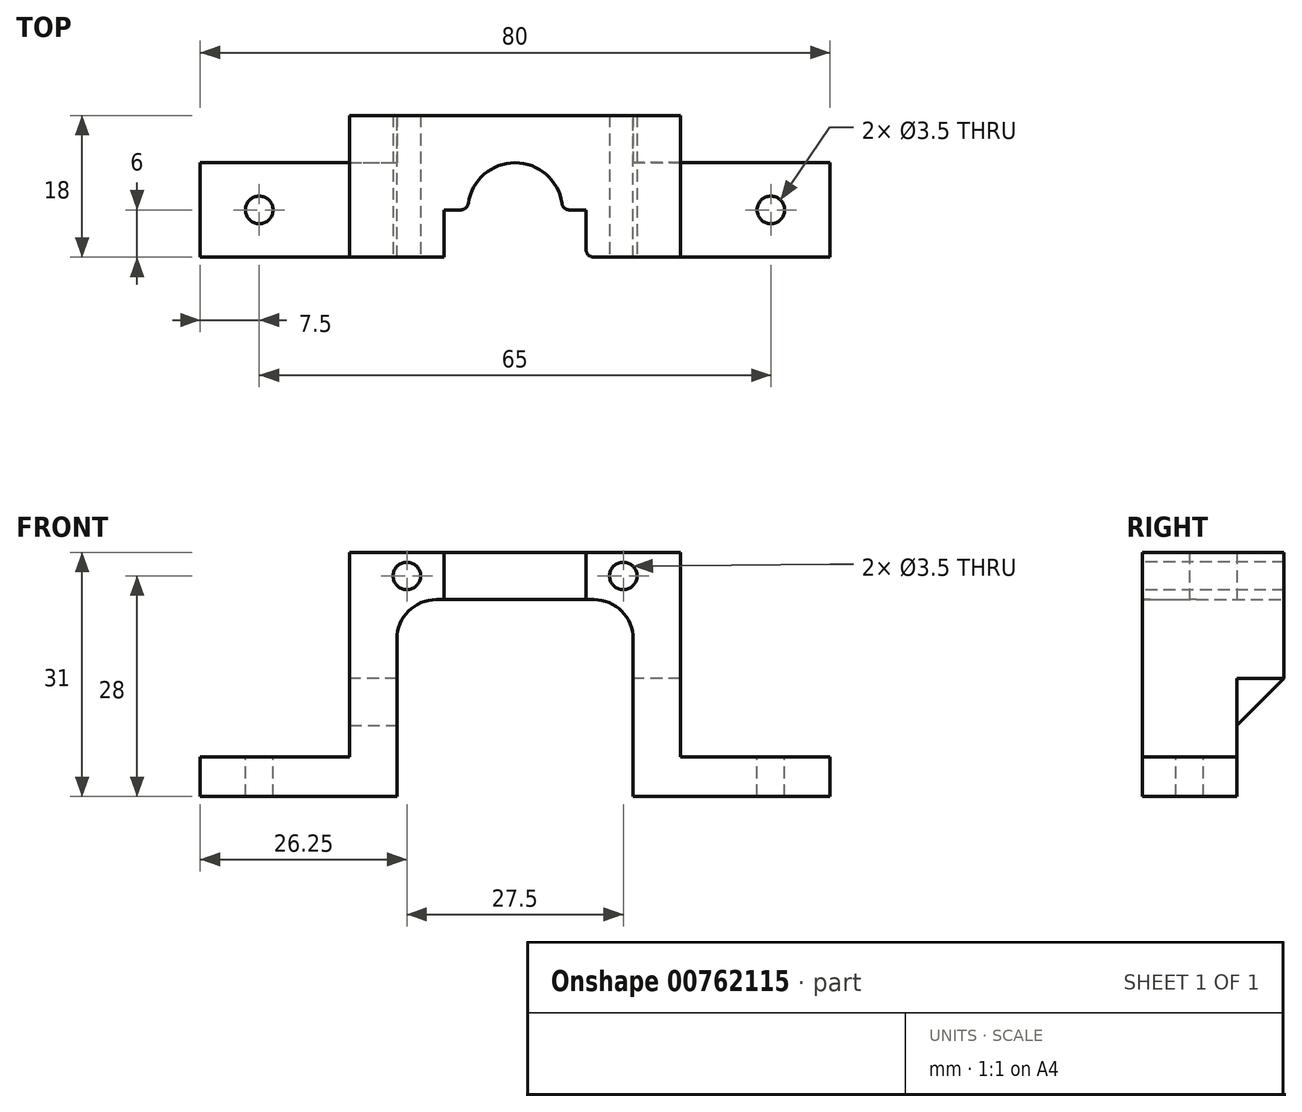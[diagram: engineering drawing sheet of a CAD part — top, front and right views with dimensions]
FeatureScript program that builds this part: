
annotation { "Feature Type Name" : "Feature", "Feature Type Description" : "" }
export const myFeature = defineFeature(function(context is Context, id is Id, definition is map)
    precondition{}
    {
        {
            var Q0;
            Q0=qCreatedBy(makeId("Front.planeOp"),FACE);
            var sketch = newSketch(context, id + "F0", { "sketchPlane" : qUnion([Q0])});
            skLineSegment(sketch, "E0", {"start": v(0, 0) * mm, "end": v(25, 0) * mm});
            skLineSegment(sketch, "E1", {"start": v(25, 0) * mm, "end": v(25, 25) * mm});
            skLineSegment(sketch, "E2", {"start": v(25, 25) * mm, "end": v(55, 25) * mm});
            skLineSegment(sketch, "E3", {"start": v(55, 25) * mm, "end": v(55, 0) * mm});
            skLineSegment(sketch, "E4", {"start": v(55, 0) * mm, "end": v(80, 0) * mm});
            skLineSegment(sketch, "E5", {"start": v(80, 0) * mm, "end": v(80, 5) * mm});
            skLineSegment(sketch, "E6", {"start": v(80, 5) * mm, "end": v(61, 5) * mm});
            skLineSegment(sketch, "E7", {"start": v(61, 5) * mm, "end": v(61, 31) * mm});
            skLineSegment(sketch, "E8", {"start": v(61, 31) * mm, "end": v(19, 31) * mm});
            skLineSegment(sketch, "E9", {"start": v(19, 31) * mm, "end": v(19, 5) * mm});
            skLineSegment(sketch, "E10", {"start": v(19, 5) * mm, "end": v(0, 5) * mm});
            skLineSegment(sketch, "E11", {"start": v(0, 5) * mm, "end": v(0, 0) * mm});
            skPoint(sketch, "E12", {"position": v(40, 25) * mm});
            skPoint(sketch, "E13", {"position": v(40, 31) * mm});
            skLineSegment(sketch, "E14", {"start": v(0, 0) * mm, "end": v(80, 0) * mm, "construction": true});
            skPoint(sketch, "E15", {"position": v(40, 0) * mm});
            skSolve(sketch);
        }
        {
            var Q0;
            Q0=makeQuery(id+"F0.imprint","IMPRINT",FACE,{"disambiguationData":[TD([[makeQuery(id+"F0.imprint","IMPRINT",EDGE,{"derivedFrom":sQuery(id+"F0.wireOp",EDGE,"E0")}),1.0]])]});
            extrude(context, id + "F1", {"entities" : qUnion([Q0]), "depth" : 12 * mm, "offsetDistance" : 25 * mm});
        }
        {
            var Q0;
            Q0=makeQuery(id+"F1.opExtrude","CAP_FACE",FACE,{"disambiguationData":[OSD([sQuery(id+"F0.wireOp",EDGE,"E0"),sQuery(id+"F0.wireOp",EDGE,"E1"),sQuery(id+"F0.wireOp",EDGE,"E2"),sQuery(id+"F0.wireOp",EDGE,"E3"),sQuery(id+"F0.wireOp",EDGE,"E4"),sQuery(id+"F0.wireOp",EDGE,"E5"),sQuery(id+"F0.wireOp",EDGE,"E6"),sQuery(id+"F0.wireOp",EDGE,"E7"),sQuery(id+"F0.wireOp",EDGE,"E8"),sQuery(id+"F0.wireOp",EDGE,"E9"),sQuery(id+"F0.wireOp",EDGE,"E10"),sQuery(id+"F0.wireOp",EDGE,"E11")])],"isStart":true});
            var sketch = newSketch(context, id + "F2", { "sketchPlane" : qUnion([Q0])});
            skLineSegment(sketch, "E16", {"start": v(-61, 15) * mm, "end": v(-55, 15) * mm});
            skLineSegment(sketch, "E17", {"start": v(-55, 15) * mm, "end": v(-55, 25) * mm});
            skLineSegment(sketch, "E18", {"start": v(-55, 25) * mm, "end": v(-25, 25) * mm});
            skLineSegment(sketch, "E19", {"start": v(-25, 25) * mm, "end": v(-25, 15) * mm});
            skPoint(sketch, "E19.endSnap0", {"position": v(-25, 12.5) * mm});
            skLineSegment(sketch, "E20", {"start": v(-25, 15) * mm, "end": v(-19, 15) * mm});
            skLineSegment(sketch, "E21", {"start": v(-19, 15) * mm, "end": v(-19, 31) * mm});
            skLineSegment(sketch, "E22", {"start": v(-19, 31) * mm, "end": v(-61, 31) * mm});
            skLineSegment(sketch, "E23", {"start": v(-61, 31) * mm, "end": v(-61, 15) * mm});
            skSolve(sketch);
        }
        {
            var Q0;
            Q0=makeQuery(id+"F2.imprint","IMPRINT",FACE,{"disambiguationData":[TD([[makeQuery(id+"F2.imprint","IMPRINT",EDGE,{"derivedFrom":sQuery(id+"F2.wireOp",EDGE,"E16")}),1.0]])]});
            extrude(context, id + "F3", {"entities" : qUnion([Q0]), "operationType" : NewBodyOperationType.ADD, "depth" : 6 * mm, "offsetDistance" : 25 * mm});
        }
        {
            var Q0;
            Q0=makeQuery(id+"F3.boolean.opBoolean","MERGE",FACE,{"derivedFrom":[makeQuery(id+"F1.opExtrude","SWEPT_FACE",FACE,{"disambiguationData":[OSD([sQuery(id+"F0.wireOp",EDGE,"E2")])]}),makeQuery(id+"F3.opExtrude","SWEPT_FACE",FACE,{"disambiguationData":[OSD([sQuery(id+"F2.wireOp",EDGE,"E18")])]})]});
            var sketch = newSketch(context, id + "F4", { "sketchPlane" : qUnion([Q0])});
            skCircle(sketch, "E24", {"center": v(40, 6) * mm, "radius": 6 * mm, "construction": true});
            skLineSegment(sketch, "E25.0.0", {"start": v(61, 12) * mm, "end": v(61, -6) * mm});
            skLineSegment(sketch, "E25.0.1", {"start": v(61, -6) * mm, "end": v(19, -6) * mm});
            skLineSegment(sketch, "E25.0.2", {"start": v(19, -6) * mm, "end": v(19, 12) * mm});
            skLineSegment(sketch, "E25.0.3", {"start": v(19, 12) * mm, "end": v(61, 12) * mm});
            skLineSegment(sketch, "E26.0.0", {"start": v(80, 0) * mm, "end": v(61, 0) * mm});
            skLineSegment(sketch, "E26.0.1", {"start": v(61, 0) * mm, "end": v(61, 12) * mm});
            skLineSegment(sketch, "E26.0.2", {"start": v(61, 12) * mm, "end": v(80, 12) * mm});
            skLineSegment(sketch, "E26.0.3", {"start": v(80, 12) * mm, "end": v(80, 0) * mm});
            skPoint(sketch, "E27", {"position": v(80, 6) * mm});
            skPoint(sketch, "E28", {"position": v(40, -6) * mm});
            skLineSegment(sketch, "E29", {"start": v(28.62, 6) * mm, "end": v(51.1, 6) * mm, "construction": true});
            skLineSegment(sketch, "E30", {"start": v(31, 12) * mm, "end": v(31, 6) * mm});
            skPoint(sketch, "E31", {"position": v(34, 6) * mm});
            skPoint(sketch, "E32", {"position": v(46, 6) * mm});
            skLineSegment(sketch, "E33", {"start": v(49, 12) * mm, "end": v(49, 6) * mm});
            skLineSegment(sketch, "E34", {"start": v(49, 6) * mm, "end": v(46, 6) * mm});
            skLineSegment(sketch, "E35", {"start": v(31, 6) * mm, "end": v(34, 6) * mm});
            skLineSegment(sketch, "E36", {"start": v(31, 12) * mm, "end": v(49, 12) * mm});
            skArc(sketch, "E37", {"start": v(34, 6) * mm, "mid": v(40, 0) * mm, "end": v(46, 6) * mm});
            skPoint(sketch, "E38", {"position": v(40, 12) * mm});
            skSolve(sketch);
        }
        {
            var Q0;
            Q0=makeQuery(id+"F4.imprint","IMPRINT",FACE,{"disambiguationData":[TD([[makeQuery(id+"F4.imprint","IMPRINT",EDGE,{"derivedFrom":sQuery(id+"F4.wireOp",EDGE,"E30")}),1.0]])]});
            extrude(context, id + "F5", {"entities" : qUnion([Q0]), "operationType" : NewBodyOperationType.REMOVE, "oppositeDirection" : true, "depth" : 25 * mm, "offsetDistance" : 25 * mm});
        }
        {
            var Q0;
            Q0=makeQuery(id+"F1.opExtrude","SWEPT_FACE",FACE,{"disambiguationData":[OSD([sQuery(id+"F0.wireOp",EDGE,"E10")])]});
            var sketch = newSketch(context, id + "F6", { "sketchPlane" : qUnion([Q0])});
            skLineSegment(sketch, "E39.0.0", {"start": v(80, 0) * mm, "end": v(61, 0) * mm});
            skLineSegment(sketch, "E39.0.1", {"start": v(61, 0) * mm, "end": v(61, -12) * mm});
            skLineSegment(sketch, "E39.0.2", {"start": v(61, -12) * mm, "end": v(80, -12) * mm});
            skLineSegment(sketch, "E39.0.3", {"start": v(80, -12) * mm, "end": v(80, 0) * mm});
            skLineSegment(sketch, "E40.0.0", {"start": v(19, 0) * mm, "end": v(0, 0) * mm});
            skLineSegment(sketch, "E40.0.1", {"start": v(0, 0) * mm, "end": v(0, -12) * mm});
            skLineSegment(sketch, "E40.0.2", {"start": v(0, -12) * mm, "end": v(19, -12) * mm});
            skLineSegment(sketch, "E40.0.3", {"start": v(19, -12) * mm, "end": v(19, 0) * mm});
            skCircle(sketch, "E41", {"center": v(7.5, -6) * mm, "radius": 1.75 * mm});
            skCircle(sketch, "E42", {"center": v(72.5, -6) * mm, "radius": 1.75 * mm});
            skPoint(sketch, "E43", {"position": v(0, -6) * mm});
            skLineSegment(sketch, "E44", {"start": v(0, 0) * mm, "end": v(80, 0) * mm, "construction": true});
            skLineSegment(sketch, "E45", {"start": v(7.5, -6) * mm, "end": v(72.5, -6) * mm, "construction": true});
            skPoint(sketch, "E46", {"position": v(40, -6) * mm});
            skPoint(sketch, "E47", {"position": v(40, 0) * mm});
            skSolve(sketch);
        }
        {
            var Q0;
            Q0=makeQuery(id+"F6.imprint","IMPRINT",FACE,{"disambiguationData":[TD([[makeQuery(id+"F6.imprint","IMPRINT",EDGE,{"derivedFrom":sQuery(id+"F6.wireOp",EDGE,"E41")}),1.0]])]});
            var Q1;
            Q1=makeQuery(id+"F6.imprint","IMPRINT",FACE,{"disambiguationData":[TD([[makeQuery(id+"F6.imprint","IMPRINT",EDGE,{"derivedFrom":sQuery(id+"F6.wireOp",EDGE,"E42")}),1.0]])]});
            extrude(context, id + "F7", {"entities" : qUnion([Q0, Q1]), "operationType" : NewBodyOperationType.REMOVE, "oppositeDirection" : true, "depth" : 25 * mm, "offsetDistance" : 25 * mm});
        }
        {
            var Q0;
            {var subQ0=sQuery(id+"F0.wireOp",EDGE,"E9");var subQ1=sQuery(id+"F0.wireOp",EDGE,"E11");var subQ2=sQuery(id+"F0.wireOp",EDGE,"E10");var subQ3=sQuery(id+"F0.wireOp",EDGE,"E0");var subQ4=sQuery(id+"F0.wireOp",EDGE,"E8");var subQ5=sQuery(id+"F0.wireOp",EDGE,"E1");var subQ6=sQuery(id+"F0.wireOp",EDGE,"E2");Q0=makeQuery(id+"F5.boolean.opBoolean","SPLIT",FACE,{"disambiguationData":[TD([makeQuery(id+"F1.opExtrude","SWEPT_FACE",FACE,{"disambiguationData":[OSD([subQ3])]})])],"derivedFrom":makeQuery(id+"F1.opExtrude","CAP_FACE",FACE,{"disambiguationData":[OSD([subQ3,subQ5,subQ6,sQuery(id+"F0.wireOp",EDGE,"E3"),sQuery(id+"F0.wireOp",EDGE,"E4"),sQuery(id+"F0.wireOp",EDGE,"E5"),sQuery(id+"F0.wireOp",EDGE,"E6"),sQuery(id+"F0.wireOp",EDGE,"E7"),subQ4,subQ0,subQ2,subQ1])],"isStart":false})});}
            var sketch = newSketch(context, id + "F8", { "sketchPlane" : qUnion([Q0])});
            skLineSegment(sketch, "E48.0.0", {"start": v(61, 31) * mm, "end": v(49, 31) * mm});
            skLineSegment(sketch, "E48.0.1", {"start": v(49, 31) * mm, "end": v(49, 25) * mm});
            skLineSegment(sketch, "E48.0.2", {"start": v(49, 25) * mm, "end": v(55, 25) * mm});
            skLineSegment(sketch, "E48.0.3", {"start": v(55, 25) * mm, "end": v(55, 0) * mm});
            skLineSegment(sketch, "E48.0.4", {"start": v(55, 0) * mm, "end": v(80, 0) * mm});
            skLineSegment(sketch, "E48.0.5", {"start": v(80, 0) * mm, "end": v(80, 5) * mm});
            skLineSegment(sketch, "E48.0.6", {"start": v(80, 5) * mm, "end": v(61, 5) * mm});
            skLineSegment(sketch, "E48.0.7", {"start": v(61, 5) * mm, "end": v(61, 31) * mm});
            skLineSegment(sketch, "E49.0.0", {"start": v(31, 25) * mm, "end": v(31, 31) * mm});
            skLineSegment(sketch, "E49.0.1", {"start": v(31, 31) * mm, "end": v(19, 31) * mm});
            skLineSegment(sketch, "E49.0.2", {"start": v(19, 31) * mm, "end": v(19, 5) * mm});
            skLineSegment(sketch, "E49.0.3", {"start": v(19, 5) * mm, "end": v(0, 5) * mm});
            skLineSegment(sketch, "E49.0.4", {"start": v(0, 5) * mm, "end": v(0, 0) * mm});
            skLineSegment(sketch, "E49.0.5", {"start": v(0, 0) * mm, "end": v(25, 0) * mm});
            skLineSegment(sketch, "E49.0.6", {"start": v(25, 0) * mm, "end": v(25, 25) * mm});
            skLineSegment(sketch, "E49.0.7", {"start": v(25, 25) * mm, "end": v(31, 25) * mm});
            skCircle(sketch, "E50", {"center": v(26.25, 28) * mm, "radius": 1.75 * mm});
            skCircle(sketch, "E51", {"center": v(53.75, 28) * mm, "radius": 1.75 * mm});
            skPoint(sketch, "E51.centerSnap0", {"position": v(31, 28) * mm});
            skLineSegment(sketch, "E52", {"start": v(26.25, 28) * mm, "end": v(53.75, 28) * mm, "construction": true});
            skPoint(sketch, "E53.0", {"position": v(40, 31) * mm});
            skPoint(sketch, "E54.0", {"position": v(49, 28) * mm});
            skPoint(sketch, "E55", {"position": v(40, 28) * mm});
            skSolve(sketch);
        }
        {
            var Q0;
            Q0=makeQuery(id+"F8.imprint","IMPRINT",FACE,{"disambiguationData":[TD([[makeQuery(id+"F8.imprint","IMPRINT",EDGE,{"derivedFrom":sQuery(id+"F8.wireOp",EDGE,"E50")}),1.0]])]});
            var Q1;
            Q1=makeQuery(id+"F8.imprint","IMPRINT",FACE,{"disambiguationData":[TD([[makeQuery(id+"F8.imprint","IMPRINT",EDGE,{"derivedFrom":sQuery(id+"F8.wireOp",EDGE,"E51")}),1.0]])]});
            extrude(context, id + "F9", {"entities" : qUnion([Q0, Q1]), "operationType" : NewBodyOperationType.REMOVE, "oppositeDirection" : true, "depth" : 25 * mm, "offsetDistance" : 25 * mm});
        }
        {
            var Q0;
            Q0=makeQuery(id+"F3.boolean.opBoolean","MERGE",EDGE,{"derivedFrom":[makeQuery(id+"F1.opExtrude","SWEPT_EDGE",EDGE,{"disambiguationData":[OSD([sQuery(id+"F0.wireOp",EDGE,"E2"),sQuery(id+"F0.wireOp",EDGE,"E3")])]}),makeQuery(id+"F3.opExtrude","SWEPT_EDGE",EDGE,{"disambiguationData":[OSD([sQuery(id+"F2.wireOp",EDGE,"E17"),sQuery(id+"F2.wireOp",EDGE,"E18")])]})]});
            var Q1;
            Q1=makeQuery(id+"F3.boolean.opBoolean","MERGE",EDGE,{"derivedFrom":[makeQuery(id+"F1.opExtrude","SWEPT_EDGE",EDGE,{"disambiguationData":[OSD([sQuery(id+"F0.wireOp",EDGE,"E1"),sQuery(id+"F0.wireOp",EDGE,"E2")])]}),makeQuery(id+"F3.opExtrude","SWEPT_EDGE",EDGE,{"disambiguationData":[OSD([sQuery(id+"F2.wireOp",EDGE,"E18"),sQuery(id+"F2.wireOp",EDGE,"E19")])]})]});
            fillet(context, id + "F10", {"entities" : qUnion([Q0, Q1]), "radius" : 5 * mm, "tangentPropagation" : true, "allowEdgeOverflow" : false});
        }
        {
            var Q0;
            Q0=makeQuery(id+"F3.opExtrude","CAP_EDGE",EDGE,{"disambiguationData":[OSD([sQuery(id+"F2.wireOp",EDGE,"E16")])],"isStart":true});
            var Q1;
            Q1=makeQuery(id+"F3.opExtrude","CAP_EDGE",EDGE,{"disambiguationData":[OSD([sQuery(id+"F2.wireOp",EDGE,"E20")])],"isStart":true});
            chamfer(context, id + "F11", {"entities" : qUnion([Q0, Q1]), "width" : 6 * mm, "tangentPropagation" : true});
        }
        {
            var Q0;
            Q0=makeQuery(id+"F5.boolean.opBoolean","COPY",EDGE,{"derivedFrom":makeQuery(id+"F5.opExtrude","SWEPT_EDGE",EDGE,{"disambiguationData":[OSD([sQuery(id+"F4.wireOp",EDGE,"E25.0.3"),sQuery(id+"F4.wireOp",EDGE,"E30"),sQuery(id+"F4.wireOp",EDGE,"E36")])]})});
            var Q1;
            Q1=makeQuery(id+"F5.boolean.opBoolean","COPY",EDGE,{"derivedFrom":makeQuery(id+"F5.opExtrude","SWEPT_EDGE",EDGE,{"disambiguationData":[OSD([sQuery(id+"F4.wireOp",EDGE,"E35"),sQuery(id+"F4.wireOp",EDGE,"E37")])]})});
            var Q2;
            Q2=makeQuery(id+"F5.boolean.opBoolean","COPY",EDGE,{"derivedFrom":makeQuery(id+"F5.opExtrude","SWEPT_EDGE",EDGE,{"disambiguationData":[OSD([sQuery(id+"F4.wireOp",EDGE,"E34"),sQuery(id+"F4.wireOp",EDGE,"E37")])]})});
            var Q3;
            Q3=makeQuery(id+"F5.boolean.opBoolean","COPY",EDGE,{"derivedFrom":makeQuery(id+"F5.opExtrude","SWEPT_EDGE",EDGE,{"disambiguationData":[OSD([sQuery(id+"F4.wireOp",EDGE,"E25.0.3"),sQuery(id+"F4.wireOp",EDGE,"E33"),sQuery(id+"F4.wireOp",EDGE,"E36")])]})});
            fillet(context, id + "F12", {"entities" : qUnion([Q0, Q1, Q2, Q3]), "radius" : 1 * mm, "tangentPropagation" : true, "allowEdgeOverflow" : false});
        }
    });
